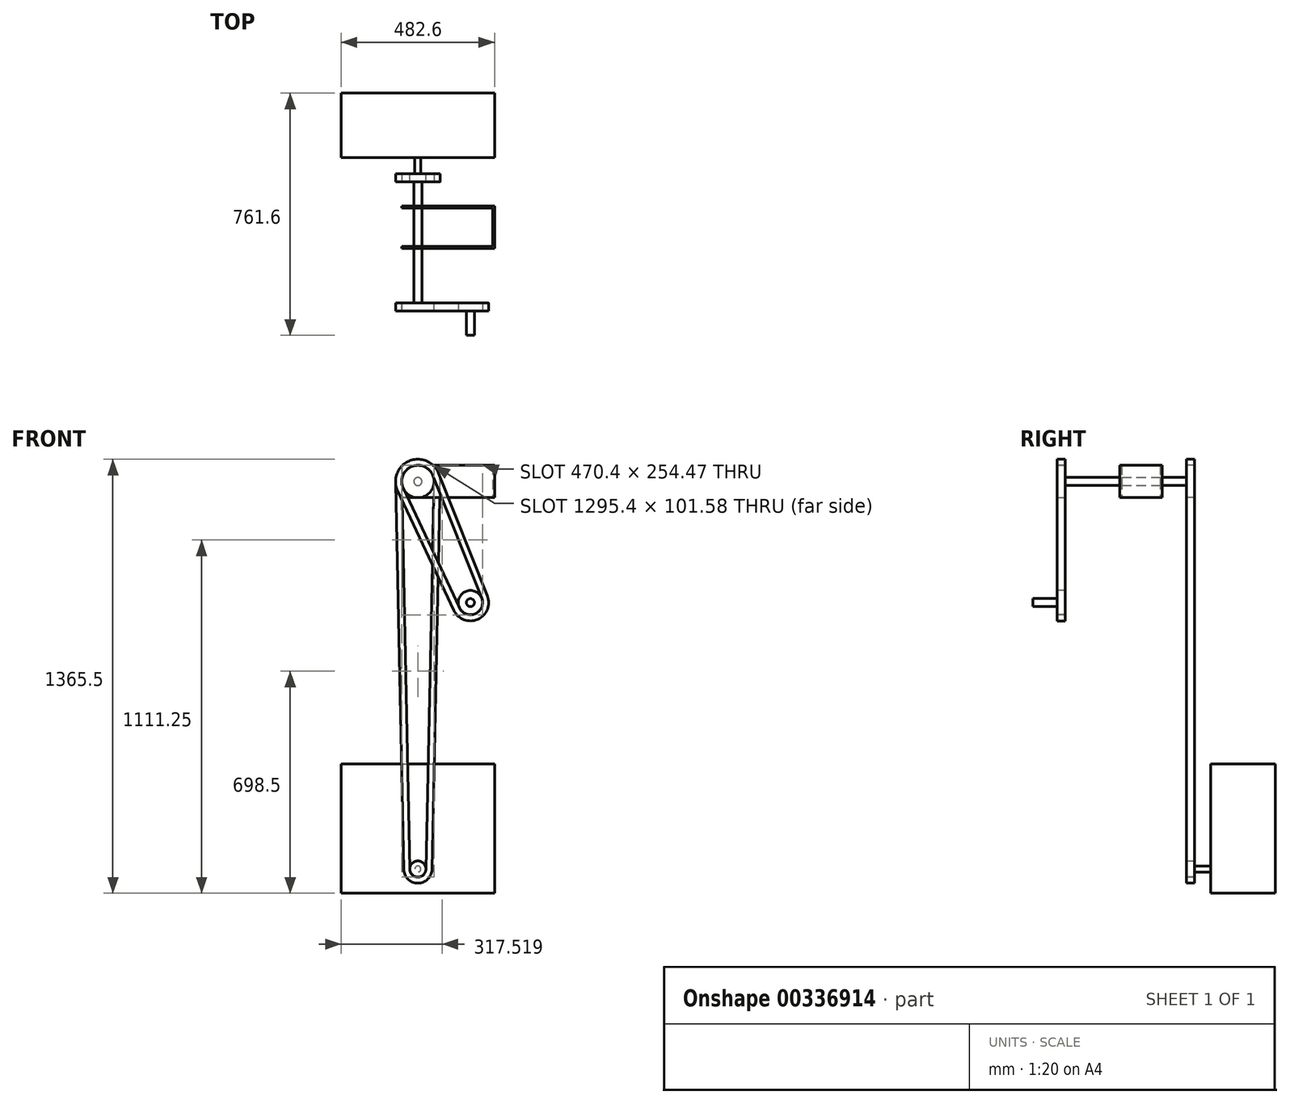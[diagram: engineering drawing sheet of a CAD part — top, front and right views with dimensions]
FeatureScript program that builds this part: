
annotation { "Feature Type Name" : "Feature", "Feature Type Description" : "" }
export const myFeature = defineFeature(function(context is Context, id is Id, definition is map)
    precondition{}
    {
        {
            var Q0;
            Q0=qCreatedBy(makeId("Front.planeOp"),FACE);
            var sketch = newSketch(context, id + "F0", { "sketchPlane" : qUnion([Q0])});
            skLineSegment(sketch, "E0.bottom", {"start": v(0, 0) * mm, "end": v(482.6, 0) * mm});
            skLineSegment(sketch, "E0.top", {"start": v(0, 406.4) * mm, "end": v(482.6, 406.4) * mm});
            skLineSegment(sketch, "E0.left", {"start": v(0, 0) * mm, "end": v(0, 406.4) * mm});
            skLineSegment(sketch, "E0.right", {"start": v(482.6, 0) * mm, "end": v(482.6, 406.4) * mm});
            skSolve(sketch);
        }
        {
            var Q0;
            Q0=makeQuery(id+"F0.imprint","IMPRINT",FACE,{"disambiguationData":[TD([[makeQuery(id+"F0.imprint","IMPRINT",EDGE,{"derivedFrom":sQuery(id+"F0.wireOp",EDGE,"E0.bottom")}),1.0]])]});
            extrude(context, id + "F1", {"entities" : qUnion([Q0]), "depth" : 203.2 * mm});
        }
        {
            var Q0;
            Q0=makeQuery(id+"F1.opExtrude","CAP_FACE",FACE,{"disambiguationData":[OSD([sQuery(id+"F0.wireOp",EDGE,"E0.bottom"),sQuery(id+"F0.wireOp",EDGE,"E0.top"),sQuery(id+"F0.wireOp",EDGE,"E0.left"),sQuery(id+"F0.wireOp",EDGE,"E0.right")])],"isStart":false});
            var sketch = newSketch(context, id + "F2", { "sketchPlane" : qUnion([Q0])});
            skCircle(sketch, "E1", {"center": v(241.3, 76.2) * mm, "radius": 9.53 * mm});
            skSolve(sketch);
        }
        {
            var Q0;
            Q0=makeQuery(id+"F2.imprint","IMPRINT",FACE,{"disambiguationData":[TD([[makeQuery(id+"F2.imprint","IMPRINT",EDGE,{"derivedFrom":sQuery(id+"F2.wireOp",EDGE,"E1")}),1.0]])]});
            extrude(context, id + "F3", {"entities" : qUnion([Q0]), "operationType" : NewBodyOperationType.ADD, "depth" : 50.8 * mm});
        }
        {
            var Q0;
            Q0=makeQuery(id+"F3.opExtrude","CAP_FACE",FACE,{"disambiguationData":[OSD([sQuery(id+"F2.wireOp",EDGE,"E1")])],"isStart":false});
            var sketch = newSketch(context, id + "F4", { "sketchPlane" : qUnion([Q0])});
            skCircle(sketch, "E2", {"center": v(241.3, 76.2) * mm, "radius": 25.4 * mm});
            skSolve(sketch);
        }
        {
            var Q0;
            Q0 = qSketchRegion(id + "F4", true);
            extrude(context, id + "F5", {"entities" : qUnion([Q0]), "operationType" : NewBodyOperationType.ADD, "depth" : 25 * mm});
        }
        {
            var Q0;
            Q0=makeQuery(id+"F5.opExtrude","CAP_FACE",FACE,{"disambiguationData":[OSD([sQuery(id+"F4.wireOp",EDGE,"E2")])],"isStart":false});
            var sketch = newSketch(context, id + "F6", { "sketchPlane" : qUnion([Q0])});
            skLineSegment(sketch, "E3", {"start": v(241.3, 76.2) * mm, "end": v(241.3, 700.75) * mm, "construction": true});
            skCircle(sketch, "E4.0", {"center": v(241.3, 76.2) * mm, "radius": 25.4 * mm, "construction": true});
            skLineSegment(sketch, "E5", {"start": v(266.7, 75.67) * mm, "end": v(292.09, 1294.34) * mm});
            skArc(sketch, "E6", {"start": v(292.09, 1294.34) * mm, "mid": v(241.3, 1346.2) * mm, "end": v(190.51, 1294.34) * mm});
            skLineSegment(sketch, "E7", {"start": v(190.51, 1294.34) * mm, "end": v(215.9, 75.67) * mm});
            skArc(sketch, "E8", {"start": v(215.9, 75.67) * mm, "mid": v(241.3, 50.8) * mm, "end": v(266.7, 75.67) * mm});
            skLineSegment(sketch, "E9.0", {"start": v(171.47, 1293.94) * mm, "end": v(196.86, 75.27) * mm});
            skArc(sketch, "E9.1", {"start": v(311.13, 1293.94) * mm, "mid": v(241.3, 1365.25) * mm, "end": v(171.47, 1293.94) * mm});
            skLineSegment(sketch, "E9.2", {"start": v(285.74, 75.27) * mm, "end": v(311.13, 1293.94) * mm});
            skArc(sketch, "E10", {"start": v(196.86, 75.27) * mm, "mid": v(241.3, 31.75) * mm, "end": v(285.74, 75.27) * mm});
            skSolve(sketch);
        }
        {
            var Q0;
            Q0=makeQuery(id+"F6.imprint","IMPRINT",FACE,{"disambiguationData":[TD([[makeQuery(id+"F6.imprint","IMPRINT",EDGE,{"derivedFrom":sQuery(id+"F6.wireOp",EDGE,"E5")}),-1.0]])]});
            extrude(context, id + "F7", {"entities" : qUnion([Q0]), "oppositeDirection" : true, "depth" : 25.4 * mm});
        }
        {
            var Q0;
            Q0=makeQuery(id+"F6.imprint","IMPRINT",FACE,{"disambiguationData":[TD([[makeQuery(id+"F6.imprint","IMPRINT",EDGE,{"derivedFrom":sQuery(id+"F6.wireOp",EDGE,"E5")}),-1.0]])]});
            var sketch = newSketch(context, id + "F8", { "sketchPlane" : qUnion([Q0])});
            skCircle(sketch, "E11", {"center": v(241.3, 1295.4) * mm, "radius": 50.8 * mm});
            skSolve(sketch);
        }
        {
            var Q0;
            Q0=makeQuery(id+"F8.imprint","IMPRINT",FACE,{"disambiguationData":[TD([[makeQuery(id+"F8.imprint","IMPRINT",EDGE,{"derivedFrom":sQuery(id+"F8.wireOp",EDGE,"E11")}),1.0]])]});
            extrude(context, id + "F9", {"entities" : qUnion([Q0]), "oppositeDirection" : true, "depth" : 25.4 * mm});
        }
        {
            var Q0;
            Q0=makeQuery(id+"F9.opExtrude","CAP_FACE",FACE,{"disambiguationData":[OSD([sQuery(id+"F8.wireOp",EDGE,"E11")])],"isStart":true});
            var sketch = newSketch(context, id + "F10", { "sketchPlane" : qUnion([Q0])});
            skSolve(sketch);
        }
        {
            var Q0;
            Q0=makeQuery(id+"F10.imprint","IMPRINT",FACE,{"disambiguationData":[TD([[makeQuery(id+"F10.imprint","IMPRINT",EDGE,{"derivedFrom":makeQuery(id+"F9.opExtrude","CAP_EDGE",EDGE,{"disambiguationData":[OSD([sQuery(id+"F8.wireOp",EDGE,"E11")])],"isStart":true})}),1.0]])]});
            var sketch = newSketch(context, id + "F11", { "sketchPlane" : qUnion([Q0])});
            skCircle(sketch, "E12", {"center": v(241.3, 1295.4) * mm, "radius": 12.7 * mm});
            skSolve(sketch);
        }
        {
            var Q0;
            Q0=makeQuery(id+"F11.imprint","IMPRINT",FACE,{"disambiguationData":[TD([[makeQuery(id+"F11.imprint","IMPRINT",EDGE,{"derivedFrom":sQuery(id+"F11.wireOp",EDGE,"E12")}),1.0]])]});
            extrude(context, id + "F12", {"entities" : qUnion([Q0]), "operationType" : NewBodyOperationType.ADD, "depth" : 381 * mm});
        }
        {
            var Q0;
            Q0=makeQuery(id+"F12.opExtrude","CAP_FACE",FACE,{"disambiguationData":[OSD([sQuery(id+"F11.wireOp",EDGE,"E12")])],"isStart":false});
            var sketch = newSketch(context, id + "F13", { "sketchPlane" : qUnion([Q0])});
            skCircle(sketch, "E13", {"center": v(241.3, 1295.4) * mm, "radius": 50.8 * mm});
            skSolve(sketch);
        }
        {
            var Q0;
            Q0 = qSketchRegion(id + "F13", true);
            extrude(context, id + "F14", {"entities" : qUnion([Q0]), "depth" : 25.4 * mm});
        }
        {
            var Q0;
            Q0=makeQuery(id+"F14.opExtrude","CAP_FACE",FACE,{"disambiguationData":[OSD([sQuery(id+"F13.wireOp",EDGE,"E13")])],"isStart":false});
            var sketch = newSketch(context, id + "F15", { "sketchPlane" : qUnion([Q0])});
            skCircle(sketch, "E14", {"center": v(406.4, 914.4) * mm, "radius": 38.1 * mm});
            skSolve(sketch);
        }
        {
            var Q0;
            Q0=makeQuery(id+"F15.imprint","IMPRINT",FACE,{"disambiguationData":[TD([[makeQuery(id+"F15.imprint","IMPRINT",EDGE,{"derivedFrom":sQuery(id+"F15.wireOp",EDGE,"E14")}),1.0]])]});
            extrude(context, id + "F16", {"entities" : qUnion([Q0]), "oppositeDirection" : true, "depth" : 25.4 * mm});
        }
        {
            var Q0;
            Q0=makeQuery(id+"F14.opExtrude","CAP_FACE",FACE,{"disambiguationData":[OSD([sQuery(id+"F13.wireOp",EDGE,"E13")])],"isStart":false});
            var sketch = newSketch(context, id + "F17", { "sketchPlane" : qUnion([Q0])});
            skArc(sketch, "E15", {"start": v(288.74, 1314.26) * mm, "mid": v(221, 1342.24) * mm, "end": v(195.1, 1273.68) * mm});
            skArc(sketch, "E16", {"start": v(371.7, 898.08) * mm, "mid": v(421.65, 879.2) * mm, "end": v(442.04, 928.57) * mm});
            skLineSegment(sketch, "E17", {"start": v(442.04, 928.57) * mm, "end": v(288.74, 1314.26) * mm});
            skLineSegment(sketch, "E18", {"start": v(371.7, 898.08) * mm, "end": v(195.1, 1273.68) * mm});
            skLineSegment(sketch, "E19.0", {"start": v(459.74, 935.6) * mm, "end": v(306.45, 1321.3) * mm});
            skArc(sketch, "E19.1", {"start": v(354.45, 889.98) * mm, "mid": v(429.22, 861.73) * mm, "end": v(459.74, 935.6) * mm});
            skLineSegment(sketch, "E19.2", {"start": v(354.45, 889.98) * mm, "end": v(177.86, 1265.57) * mm});
            skArc(sketch, "E19.3", {"start": v(306.45, 1321.3) * mm, "mid": v(213.43, 1359.72) * mm, "end": v(177.86, 1265.57) * mm});
            skSolve(sketch);
        }
        {
            var Q0;
            Q0=makeQuery(id+"F17.imprint","IMPRINT",FACE,{"disambiguationData":[TD([[makeQuery(id+"F17.imprint","IMPRINT",EDGE,{"derivedFrom":sQuery(id+"F17.wireOp",EDGE,"E15")}),-1.0]])]});
            extrude(context, id + "F18", {"entities" : qUnion([Q0]), "oppositeDirection" : true, "depth" : 25.4 * mm});
        }
        {
            var Q0;
            Q0=makeQuery(id+"F16.opExtrude","CAP_FACE",FACE,{"disambiguationData":[OSD([sQuery(id+"F15.wireOp",EDGE,"E14")])],"isStart":true});
            var sketch = newSketch(context, id + "F19", { "sketchPlane" : qUnion([Q0])});
            skCircle(sketch, "E20", {"center": v(406.4, 914.4) * mm, "radius": 12.7 * mm});
            skSolve(sketch);
        }
        {
            var Q0;
            Q0=makeQuery(id+"F19.imprint","IMPRINT",FACE,{"disambiguationData":[TD([[makeQuery(id+"F19.imprint","IMPRINT",EDGE,{"derivedFrom":sQuery(id+"F19.wireOp",EDGE,"E20")}),1.0]])]});
            extrude(context, id + "F20", {"entities" : qUnion([Q0]), "operationType" : NewBodyOperationType.ADD, "depth" : 76.2 * mm});
        }
        {
            var Q0;
            Q0=makeQuery(id+"F14.opExtrude","CAP_FACE",FACE,{"disambiguationData":[OSD([sQuery(id+"F13.wireOp",EDGE,"E13")])],"isStart":false});
            cPlane(context, id + "F21", {"entities" : qUnion([Q0]), "cplaneType" : CPlaneType.OFFSET, "offset" : 203.2 * mm, "oppositeDirection" : true, "width" : 152.4 * mm, "height" : 152.4 * mm});
        }
        {
            var Q0;
            Q0=qCreatedBy(id+"F21.planeOp",FACE);
            var sketch = newSketch(context, id + "F22", { "sketchPlane" : qUnion([Q0])});
            skLineSegment(sketch, "E21.bottom", {"start": v(190.25, 1346.45) * mm, "end": v(476.25, 1346.45) * mm});
            skLineSegment(sketch, "E21.top", {"start": v(190.25, 1244.85) * mm, "end": v(476.25, 1244.85) * mm});
            skLineSegment(sketch, "E21.left", {"start": v(190.25, 1346.45) * mm, "end": v(190.25, 1244.85) * mm});
            skCircle(sketch, "E22", {"center": v(241.3, 1295.4) * mm, "radius": 12.7 * mm});
            skLineSegment(sketch, "E23", {"start": v(476.25, 1346.45) * mm, "end": v(476.25, 1244.85) * mm});
            skSolve(sketch);
        }
        {
            var Q0;
            Q0=makeQuery(id+"F22.imprint","IMPRINT",FACE,{"disambiguationData":[TD([[makeQuery(id+"F22.imprint","IMPRINT",EDGE,{"derivedFrom":sQuery(id+"F22.wireOp",EDGE,"E21.bottom")}),-1.0]])]});
            extrude(context, id + "F23", {"entities" : qUnion([Q0]), "operationType" : NewBodyOperationType.ADD, "depth" : 6.35 * mm});
        }
        {
            var Q0;
            Q0=makeQuery(id+"F23.opExtrude","SWEPT_FACE",FACE,{"disambiguationData":[OSD([sQuery(id+"F22.wireOp",EDGE,"E23")])]});
            var sketch = newSketch(context, id + "F24", { "sketchPlane" : qUnion([Q0])});
            skLineSegment(sketch, "E24.bottom", {"start": v(-488.55, 1346.45) * mm, "end": v(-361.55, 1346.45) * mm});
            skLineSegment(sketch, "E24.top", {"start": v(-488.55, 1244.85) * mm, "end": v(-361.55, 1244.85) * mm});
            skLineSegment(sketch, "E24.left", {"start": v(-488.55, 1346.45) * mm, "end": v(-488.55, 1244.85) * mm});
            skLineSegment(sketch, "E24.right", {"start": v(-361.55, 1346.45) * mm, "end": v(-361.55, 1244.85) * mm});
            skSolve(sketch);
        }
        {
            var Q0;
            Q0 = qSketchRegion(id + "F24", true);
            extrude(context, id + "F25", {"entities" : qUnion([Q0]), "operationType" : NewBodyOperationType.ADD, "depth" : 6.35 * mm});
        }
        {
            var Q0;
            Q0=makeQuery(id+"F25.opExtrude","SWEPT_FACE",FACE,{"disambiguationData":[OSD([sQuery(id+"F24.wireOp",EDGE,"E24.right")])]});
            var sketch = newSketch(context, id + "F26", { "sketchPlane" : qUnion([Q0])});
            skLineSegment(sketch, "E25.bottom", {"start": v(-482.6, 1346.45) * mm, "end": v(-190.25, 1346.45) * mm});
            skLineSegment(sketch, "E25.top", {"start": v(-482.6, 1244.85) * mm, "end": v(-190.25, 1244.85) * mm});
            skLineSegment(sketch, "E25.left", {"start": v(-482.6, 1346.45) * mm, "end": v(-482.6, 1244.85) * mm});
            skLineSegment(sketch, "E25.right", {"start": v(-190.25, 1346.45) * mm, "end": v(-190.25, 1244.85) * mm});
            skSolve(sketch);
        }
        {
            var Q0;
            Q0 = qSketchRegion(id + "F26", true);
            extrude(context, id + "F27", {"entities" : qUnion([Q0]), "operationType" : NewBodyOperationType.ADD, "depth" : 6.35 * mm});
        }
    });
